# Revit family: Sink-Corian-Sweet-809
name_source: partatom
category: Plumbing Fixtures
revit_build: Autodesk Revit 2015 (Build: 20140606_1530(x64)
units: mm (PartAtom-declared; Revit-internal decimal feet)

## types (1)
- 809
    CWFU = 0
    Cost = 0 $
    Default Elevation = 1219 mm
    Depth = 181 mm
    Description = Kitchen Sink Europe Specification
    Finish = Solid Surface Sink - DuPont - Bone
    HWFU = 0
    Interior Length = 316 mm  [stored 1.03675 ft]
    Interior Width = 265 mm  [stored 0.869423 ft]
    Length = 368 mm  [stored 1.20735 ft]
    Manufacturer = DuPont
    Model = Sweet 809
    Product Page URL = http://www.dupont.co.uk
    Sink Colors Available = Bone, Cameo White, Designer White, Glacier White, Vanilla
    URL = http://www.dupont.com
    Version = 2014 - v1.0a
    WFU = 0
    Width = 318 mm  [stored 1.04331 ft]

note: [stored X ft] marks values corroborated as IEEE doubles in the binary element streams (Revit-internal decimal feet)

## geometry (parser evidence)
native form markers: Sweep x2
no freeform markers — native parametric forms only
